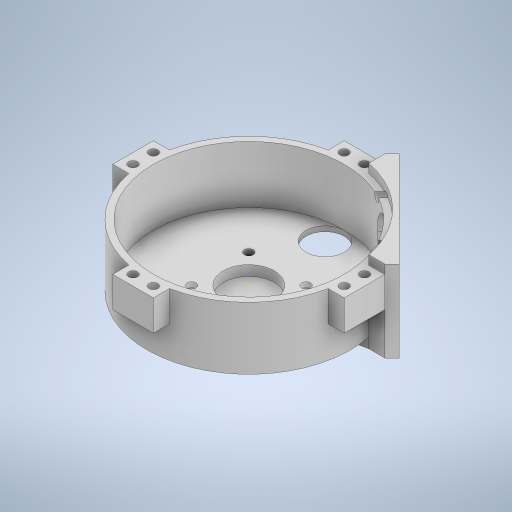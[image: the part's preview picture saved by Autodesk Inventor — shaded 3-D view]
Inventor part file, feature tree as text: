
AUTODESK INVENTOR PART (.ipt)
format: ipt  version: 2023 (Build 270158000, 158)  size: 517,632 bytes
history: native  units: in
note: dims shown in document units (in); Inventor stores cm internally (conversion verified against a paired STEP export)
features: sketch x19, extrude x15, hole x3
ambient origin geometry x8: Origin, YZ Plane, XZ Plane, XY Plane, X Axis, Y Axis, Z Axis, Center Point
bodies: Solid1 (feature_tree)
feature tree (37):
  extrude  "Extrusion1"  Depth=1.375in TaperAngle=0.0deg
  extrude  "Extrusion2"  Depth=1.275in TaperAngle=0.0deg
  extrude  "Extrusion3"  Depth=1.125in TaperAngle=0.0deg
  hole  "Hole1"  [1 undecoded]
  extrude  "Extrusion4"  Depth=0.4in
  extrude  "Extrusion5"  Depth=0.4in
  hole  "Hole2"  [1 undecoded]
  extrude  "Extrusion6"  Depth=0.4in
  sketch  "Sketch10"  dims[d26=0.8in d27=0.4in]
  extrude  "Extrusion7"  Depth=0.4in
  extrude  "Extrusion8"  Depth=0.8in
  extrude  "Extrusion9"  Depth=0.4in
  extrude  "Extrusion11"  Depth=0.75in TaperAngle=0.0deg
  extrude  "Extrusion12"  Depth=0.2in
  extrude  "Extrusion13"  Depth=0.2in
  extrude  "Extrusion14"  Depth=0.4in
  extrude  "Extrusion16"  Depth=0.2in
  hole  "Hole5"  [1 undecoded]
  extrude  "Extrusion17"  Depth=1.2in
  sketch  "Sketch1"  dims[d0=4.0in d1=1.375in d2=0.0in]
  sketch  "Sketch2"  dims[d3=3.75in d4=1.275in d5=0.0in]
  sketch  "Sketch3"  dims[d6=1.0in d7=1.125in d8=0.0in]
  sketch  "Sketch4"  dims[d9=1.125in d10=1.125in]
  sketch  "Sketch5"  dims[d11=0.177in d12=0.75in d13=0.332in d14=0.25in d15=0.5635in d16=1.0in d17=0.8108in d18=0.4in]
  sketch  "Sketch6"  dims[d19=0.4in d20=0.4in]
  sketch  "Sketch7"  dims[d21=0.4in d22=0.75in d23=0.0in]
  sketch  "Sketch8"  dims[d24=0.4in d25=0.4in]
  sketch  "Sketch11"  dims[d28=0.4in d29=0.8in]
  sketch  "Sketch12"  dims[d30=0.4in d31=0.4in]
  sketch  "Sketch13"  dims[d32=0.8in d33=0.75in d34=0.0in]
  sketch  "Sketch17"  dims[d35=0.2in d36=0.2in]
  sketch  "Sketch18"  dims[d37=0.4in d38=0.2in]
  sketch  "Sketch19"  dims[d39=0.2in d40=0.4in]
  sketch  "Sketch20"  dims[d41=0.2in d42=0.2in]
  sketch  "Sketch23"  dims[d43=0.2in d44=0.2in]
  sketch  "Sketch24"  dims[d45=0.4in]
  sketch  "Sketch25"  dims[d46=0.177in d47=0.75in d48=0.375in d49=0.25in d50=0.5635in d51=0.75in d52=0.8108in d53=1.5in d54=0.75in d55=0.0in d66=0.15in d67=0.0in d68=2.0in d69=0.275in d70=0.275in d71=0.275in d72=0.275in d73=0.1in d74=0.0in d75=0.1in d76=0.0in d79=0.175in d80=0.0in d81=0.2in d82=0.175in d83=0.0in d84=0.2in d85=0.0in d86=1.0875in d87=0.0in d101=1.425in d102=0.0in d103=1.425in d104=0.0in d105=0.3in d106=0.0in d107=0.8in d108=1.326in d109=1.18in d110=1.18in d111=0.169in d112=0.75in d113=0.375in d114=0.25in d115=0.5635in d116=0.75in d117=0.8108in d118=0.75in d119=1.2in d120=0.3in d121=0.0in]
note: 3 required parameter values undecoded (feature->parameter linkage not recoverable at this tier; creation-order binding heuristic only, values carry confidence <= 0.55)
